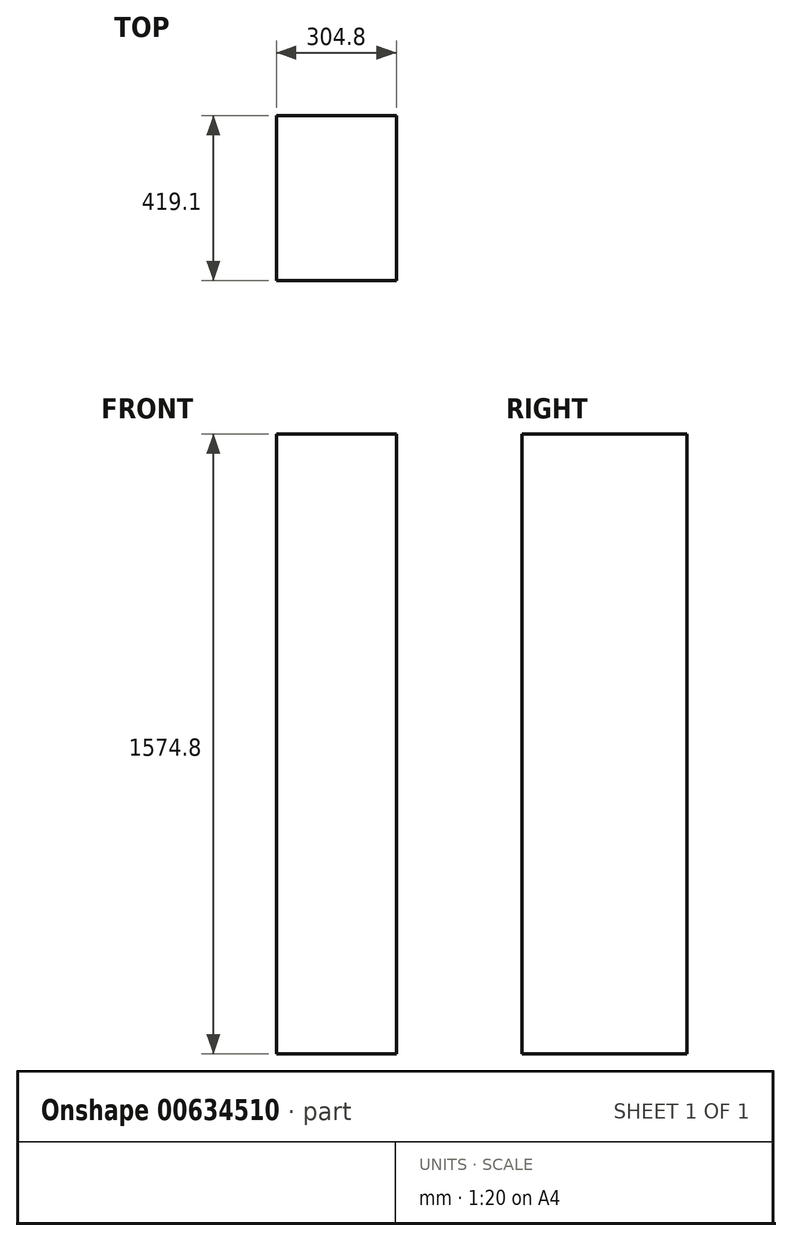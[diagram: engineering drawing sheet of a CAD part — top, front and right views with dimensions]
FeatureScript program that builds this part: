
annotation { "Feature Type Name" : "Feature", "Feature Type Description" : "" }
export const myFeature = defineFeature(function(context is Context, id is Id, definition is map)
    precondition{}
    {
        {
            var Q0;
            Q0=qCreatedBy(makeId("Top.planeOp"),FACE);
            var sketch = newSketch(context, id + "F0", { "sketchPlane" : qUnion([Q0])});
            skLineSegment(sketch, "E0.bottom", {"start": v(-152.4, -209.55) * mm, "end": v(152.4, -209.55) * mm});
            skLineSegment(sketch, "E0.top", {"start": v(-152.4, 209.55) * mm, "end": v(152.4, 209.55) * mm});
            skLineSegment(sketch, "E0.left", {"start": v(-152.4, -209.55) * mm, "end": v(-152.4, 209.55) * mm});
            skLineSegment(sketch, "E0.right", {"start": v(152.4, -209.55) * mm, "end": v(152.4, 209.55) * mm});
            skPoint(sketch, "E0.middle", {"position": v(0, 0) * mm});
            skSolve(sketch);
        }
        {
            var Q0;
            Q0=makeQuery(id+"F0.imprint","IMPRINT",FACE,{"disambiguationData":[TD([[makeQuery(id+"F0.imprint","IMPRINT",EDGE,{"derivedFrom":sQuery(id+"F0.wireOp",EDGE,"E0.bottom")}),1.0]])]});
            extrude(context, id + "F1", {"entities" : qUnion([Q0]), "depth" : 1574.8 * mm});
        }
    });
